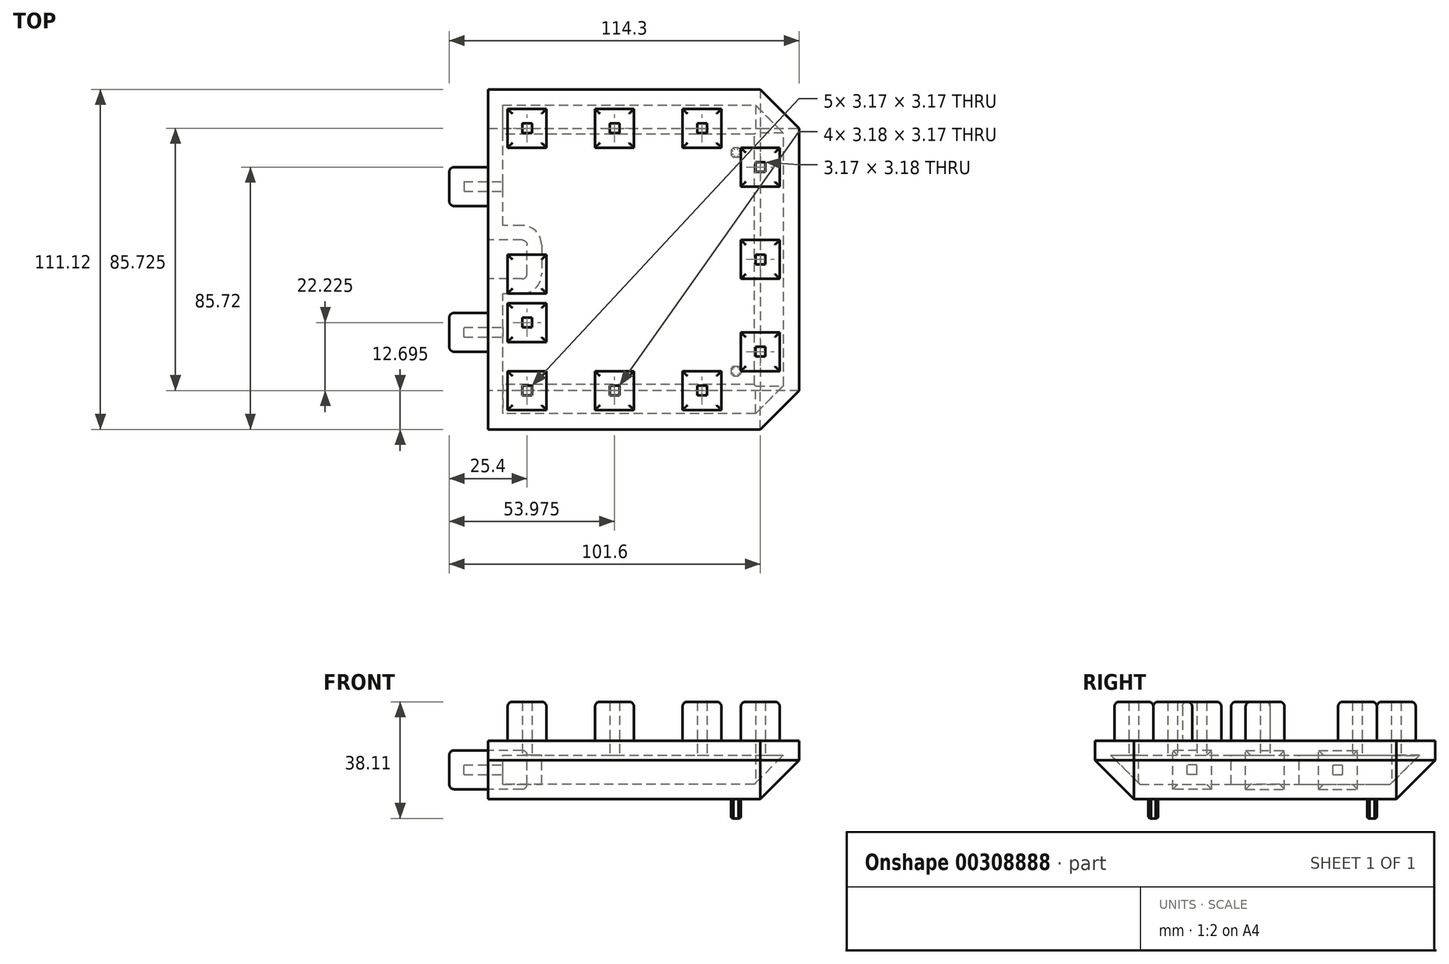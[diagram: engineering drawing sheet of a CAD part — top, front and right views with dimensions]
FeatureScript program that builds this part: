
annotation { "Feature Type Name" : "Feature", "Feature Type Description" : "" }
export const myFeature = defineFeature(function(context is Context, id is Id, definition is map)
    precondition{}
    {
        {
            var Q0;
            Q0=qCreatedBy(makeId("Front.planeOp"),FACE);
            var sketch = newSketch(context, id + "F0", { "sketchPlane" : qUnion([Q0])});
            skLineSegment(sketch, "E0.bottom", {"start": v(-50.8, -9.53) * mm, "end": v(50.8, -9.53) * mm});
            skLineSegment(sketch, "E0.top", {"start": v(-50.8, 9.53) * mm, "end": v(50.8, 9.53) * mm});
            skLineSegment(sketch, "E0.left", {"start": v(-50.8, -9.53) * mm, "end": v(-50.8, 9.53) * mm});
            skLineSegment(sketch, "E0.right", {"start": v(50.8, -9.53) * mm, "end": v(50.8, 9.53) * mm});
            skPoint(sketch, "E0.middle", {"position": v(0, 0) * mm});
            skSolve(sketch);
        }
        {
            var Q0;
            Q0 = qSketchRegion(id + "F0", true);
            extrude(context, id + "F1", {"entities" : qUnion([Q0]), "depth" : 111.12 * mm});
        }
        {
            var Q0;
            Q0=makeQuery(id+"F1.opExtrude","SWEPT_EDGE",EDGE,{"disambiguationData":[OSD([sQuery(id+"F0.wireOp",EDGE,"E0.bottom"),sQuery(id+"F0.wireOp",EDGE,"E0.right")])]});
            var Q1;
            Q1=makeQuery(id+"F1.opExtrude","CAP_EDGE",EDGE,{"disambiguationData":[OSD([sQuery(id+"F0.wireOp",EDGE,"E0.bottom")])],"isStart":false});
            var Q2;
            Q2=makeQuery(id+"F1.opExtrude","CAP_EDGE",EDGE,{"disambiguationData":[OSD([sQuery(id+"F0.wireOp",EDGE,"E0.bottom")])],"isStart":true});
            var Q3;
            Q3=makeQuery(id+"F1.opExtrude","CAP_EDGE",EDGE,{"disambiguationData":[OSD([sQuery(id+"F0.wireOp",EDGE,"E0.right")])],"isStart":false});
            var Q4;
            Q4=makeQuery(id+"F1.opExtrude","CAP_EDGE",EDGE,{"disambiguationData":[OSD([sQuery(id+"F0.wireOp",EDGE,"E0.right")])],"isStart":true});
            chamfer(context, id + "F2", {"entities" : qUnion([Q0, Q1, Q2, Q3, Q4]), "width" : 12.7 * mm, "tangentPropagation" : true});
        }
        {
            var Q0;
            Q0=makeQuery(id+"F1.opExtrude","SWEPT_FACE",FACE,{"disambiguationData":[OSD([sQuery(id+"F0.wireOp",EDGE,"E0.top")])]});
            var sketch = newSketch(context, id + "F3", { "sketchPlane" : qUnion([Q0])});
            skLineSegment(sketch, "E1.bottom", {"start": v(31.75, -31.75) * mm, "end": v(44.45, -31.75) * mm});
            skLineSegment(sketch, "E1.top", {"start": v(31.75, -19.05) * mm, "end": v(44.45, -19.05) * mm});
            skLineSegment(sketch, "E1.left", {"start": v(31.75, -31.75) * mm, "end": v(31.75, -19.05) * mm});
            skLineSegment(sketch, "E1.right", {"start": v(44.45, -31.75) * mm, "end": v(44.45, -19.05) * mm});
            skPoint(sketch, "E1.middle", {"position": v(38.1, -25.4) * mm});
            skLineSegment(sketch, "E2.bottom", {"start": v(31.75, -92.08) * mm, "end": v(44.45, -92.08) * mm});
            skLineSegment(sketch, "E2.top", {"start": v(31.75, -79.38) * mm, "end": v(44.45, -79.38) * mm});
            skLineSegment(sketch, "E2.left", {"start": v(31.75, -92.08) * mm, "end": v(31.75, -79.38) * mm});
            skLineSegment(sketch, "E2.right", {"start": v(44.45, -92.08) * mm, "end": v(44.45, -79.38) * mm});
            skPoint(sketch, "E2.middle", {"position": v(38.1, -85.73) * mm});
            skLineSegment(sketch, "E3.bottom", {"start": v(31.75, -61.91) * mm, "end": v(44.45, -61.91) * mm});
            skLineSegment(sketch, "E3.top", {"start": v(31.75, -49.21) * mm, "end": v(44.45, -49.21) * mm});
            skLineSegment(sketch, "E3.left", {"start": v(31.75, -61.91) * mm, "end": v(31.75, -49.21) * mm});
            skLineSegment(sketch, "E3.right", {"start": v(44.45, -61.91) * mm, "end": v(44.45, -49.21) * mm});
            skPoint(sketch, "E3.middle", {"position": v(38.1, -55.56) * mm});
            skLineSegment(sketch, "E4.bottom", {"start": v(12.7, -19.05) * mm, "end": v(25.4, -19.05) * mm});
            skLineSegment(sketch, "E4.top", {"start": v(12.7, -6.35) * mm, "end": v(25.4, -6.35) * mm});
            skLineSegment(sketch, "E4.left", {"start": v(12.7, -19.05) * mm, "end": v(12.7, -6.35) * mm});
            skLineSegment(sketch, "E4.right", {"start": v(25.4, -19.05) * mm, "end": v(25.4, -6.35) * mm});
            skPoint(sketch, "E4.middle", {"position": v(19.05, -12.7) * mm});
            skLineSegment(sketch, "E5.bottom", {"start": v(12.7, -92.08) * mm, "end": v(25.4, -92.08) * mm});
            skLineSegment(sketch, "E5.top", {"start": v(12.7, -104.78) * mm, "end": v(25.4, -104.78) * mm});
            skLineSegment(sketch, "E5.left", {"start": v(12.7, -92.08) * mm, "end": v(12.7, -104.78) * mm});
            skLineSegment(sketch, "E5.right", {"start": v(25.4, -92.08) * mm, "end": v(25.4, -104.78) * mm});
            skPoint(sketch, "E5.middle", {"position": v(19.05, -98.43) * mm});
            skLineSegment(sketch, "E6.bottom", {"start": v(-15.88, -19.05) * mm, "end": v(-3.18, -19.05) * mm});
            skLineSegment(sketch, "E6.top", {"start": v(-15.88, -6.35) * mm, "end": v(-3.18, -6.35) * mm});
            skLineSegment(sketch, "E6.left", {"start": v(-15.88, -19.05) * mm, "end": v(-15.88, -6.35) * mm});
            skLineSegment(sketch, "E6.right", {"start": v(-3.18, -19.05) * mm, "end": v(-3.18, -6.35) * mm});
            skPoint(sketch, "E6.middle", {"position": v(-9.53, -12.7) * mm});
            skLineSegment(sketch, "E7.bottom", {"start": v(-15.88, -92.08) * mm, "end": v(-3.18, -92.08) * mm});
            skLineSegment(sketch, "E7.top", {"start": v(-15.88, -104.78) * mm, "end": v(-3.18, -104.78) * mm});
            skLineSegment(sketch, "E7.left", {"start": v(-15.88, -92.08) * mm, "end": v(-15.88, -104.78) * mm});
            skLineSegment(sketch, "E7.right", {"start": v(-3.18, -92.08) * mm, "end": v(-3.18, -104.78) * mm});
            skPoint(sketch, "E7.middle", {"position": v(-9.53, -98.43) * mm});
            skLineSegment(sketch, "E8.bottom", {"start": v(-31.75, -19.05) * mm, "end": v(-44.45, -19.05) * mm});
            skLineSegment(sketch, "E8.top", {"start": v(-31.75, -6.35) * mm, "end": v(-44.45, -6.35) * mm});
            skLineSegment(sketch, "E8.left", {"start": v(-31.75, -19.05) * mm, "end": v(-31.75, -6.35) * mm});
            skLineSegment(sketch, "E8.right", {"start": v(-44.45, -19.05) * mm, "end": v(-44.45, -6.35) * mm});
            skPoint(sketch, "E8.middle", {"position": v(-38.1, -12.7) * mm});
            skPoint(sketch, "E8.middle.positionSnap0", {"position": v(-15.88, -12.7) * mm});
            skPoint(sketch, "E8.centerSnap0", {"position": v(-15.88, -12.7) * mm});
            skLineSegment(sketch, "E9.bottom", {"start": v(-31.75, -104.78) * mm, "end": v(-44.45, -104.78) * mm});
            skLineSegment(sketch, "E9.top", {"start": v(-31.75, -92.08) * mm, "end": v(-44.45, -92.08) * mm});
            skLineSegment(sketch, "E9.left", {"start": v(-31.75, -104.78) * mm, "end": v(-31.75, -92.08) * mm});
            skLineSegment(sketch, "E9.right", {"start": v(-44.45, -104.78) * mm, "end": v(-44.45, -92.08) * mm});
            skPoint(sketch, "E9.middle", {"position": v(-38.1, -98.43) * mm});
            skPoint(sketch, "E9.middle.positionSnap0", {"position": v(-15.88, -98.43) * mm});
            skPoint(sketch, "E9.centerSnap0", {"position": v(-15.88, -98.43) * mm});
            skSolve(sketch);
        }
        {
            var Q0;
            Q0 = qSketchRegion(id + "F3", true);
            extrude(context, id + "F4", {"entities" : qUnion([Q0]), "operationType" : NewBodyOperationType.ADD, "depth" : 12.7 * mm});
        }
        {
            var Q0;
            Q0=makeQuery(id+"F1.opExtrude","SWEPT_FACE",FACE,{"disambiguationData":[OSD([sQuery(id+"F0.wireOp",EDGE,"E0.bottom")])]});
            var sketch = newSketch(context, id + "F5", { "sketchPlane" : qUnion([Q0])});
            skLineSegment(sketch, "E10.bottom", {"start": v(28.58, 90.49) * mm, "end": v(31.75, 90.49) * mm});
            skLineSegment(sketch, "E10.top", {"start": v(28.58, 93.66) * mm, "end": v(31.75, 93.66) * mm});
            skLineSegment(sketch, "E10.left", {"start": v(28.58, 90.49) * mm, "end": v(28.58, 93.66) * mm});
            skLineSegment(sketch, "E10.right", {"start": v(31.75, 90.49) * mm, "end": v(31.75, 93.66) * mm});
            skPoint(sketch, "E10.middle", {"position": v(30.16, 92.08) * mm});
            skLineSegment(sketch, "E11.bottom", {"start": v(31.75, 19.05) * mm, "end": v(28.58, 19.05) * mm});
            skLineSegment(sketch, "E11.top", {"start": v(31.75, 22.22) * mm, "end": v(28.58, 22.22) * mm});
            skLineSegment(sketch, "E11.left", {"start": v(31.75, 19.05) * mm, "end": v(31.75, 22.23) * mm});
            skLineSegment(sketch, "E11.right", {"start": v(28.58, 19.05) * mm, "end": v(28.58, 22.23) * mm});
            skPoint(sketch, "E11.middle", {"position": v(30.16, 20.64) * mm});
            skSolve(sketch);
        }
        {
            var Q0;
            Q0 = qSketchRegion(id + "F5", true);
            extrude(context, id + "F6", {"entities" : qUnion([Q0]), "operationType" : NewBodyOperationType.ADD, "depth" : 6.35 * mm});
        }
        {
            var Q0;
            Q0=makeQuery(id+"F6.opExtrude","SWEPT_EDGE",EDGE,{"disambiguationData":[OSD([sQuery(id+"F5.wireOp",EDGE,"E11.bottom"),sQuery(id+"F5.wireOp",EDGE,"E11.right")])]});
            var Q1;
            Q1=makeQuery(id+"F6.opExtrude","SWEPT_EDGE",EDGE,{"disambiguationData":[OSD([sQuery(id+"F5.wireOp",EDGE,"E11.top"),sQuery(id+"F5.wireOp",EDGE,"E11.right")])]});
            var Q2;
            Q2=makeQuery(id+"F6.opExtrude","SWEPT_EDGE",EDGE,{"disambiguationData":[OSD([sQuery(id+"F5.wireOp",EDGE,"E11.top"),sQuery(id+"F5.wireOp",EDGE,"E11.left")])]});
            var Q3;
            Q3=makeQuery(id+"F6.opExtrude","SWEPT_EDGE",EDGE,{"disambiguationData":[OSD([sQuery(id+"F5.wireOp",EDGE,"E11.bottom"),sQuery(id+"F5.wireOp",EDGE,"E11.left")])]});
            var Q4;
            Q4=makeQuery(id+"F6.opExtrude","CAP_EDGE",EDGE,{"disambiguationData":[OSD([sQuery(id+"F5.wireOp",EDGE,"E11.left")])],"isStart":true});
            var Q5;
            Q5=makeQuery(id+"F6.opExtrude","SWEPT_EDGE",EDGE,{"disambiguationData":[OSD([sQuery(id+"F5.wireOp",EDGE,"E10.bottom"),sQuery(id+"F5.wireOp",EDGE,"E10.left")])]});
            var Q6;
            Q6=makeQuery(id+"F6.opExtrude","SWEPT_EDGE",EDGE,{"disambiguationData":[OSD([sQuery(id+"F5.wireOp",EDGE,"E10.bottom"),sQuery(id+"F5.wireOp",EDGE,"E10.right")])]});
            var Q7;
            Q7=makeQuery(id+"F6.opExtrude","SWEPT_EDGE",EDGE,{"disambiguationData":[OSD([sQuery(id+"F5.wireOp",EDGE,"E10.top"),sQuery(id+"F5.wireOp",EDGE,"E10.right")])]});
            var Q8;
            Q8=makeQuery(id+"F6.opExtrude","CAP_EDGE",EDGE,{"disambiguationData":[OSD([sQuery(id+"F5.wireOp",EDGE,"E10.right")])],"isStart":true});
            var Q9;
            Q9=makeQuery(id+"F6.opExtrude","SWEPT_EDGE",EDGE,{"disambiguationData":[OSD([sQuery(id+"F5.wireOp",EDGE,"E10.top"),sQuery(id+"F5.wireOp",EDGE,"E10.left")])]});
            chamfer(context, id + "F7", {"entities" : qUnion([Q0, Q1, Q2, Q3, Q4, Q5, Q6, Q7, Q8, Q9]), "width" : 0.8 * mm, "tangentPropagation" : true});
        }
        {
            var Q0;
            Q0=makeQuery(id+"F6.opExtrude","CAP_FACE",FACE,{"disambiguationData":[OSD([sQuery(id+"F5.wireOp",EDGE,"E10.bottom"),sQuery(id+"F5.wireOp",EDGE,"E10.top"),sQuery(id+"F5.wireOp",EDGE,"E10.left"),sQuery(id+"F5.wireOp",EDGE,"E10.right")])],"isStart":false});
            var Q1;
            Q1=makeQuery(id+"F6.opExtrude","CAP_FACE",FACE,{"disambiguationData":[OSD([sQuery(id+"F5.wireOp",EDGE,"E11.bottom"),sQuery(id+"F5.wireOp",EDGE,"E11.top"),sQuery(id+"F5.wireOp",EDGE,"E11.left"),sQuery(id+"F5.wireOp",EDGE,"E11.right")])],"isStart":false});
            fillet(context, id + "F8", {"entities" : qUnion([Q0, Q1]), "radius" : 0.64 * mm, "tangentPropagation" : true, "allowEdgeOverflow" : false});
        }
        {
            var Q0;
            Q0=makeQuery(id+"F1.opExtrude","SWEPT_FACE",FACE,{"disambiguationData":[OSD([sQuery(id+"F0.wireOp",EDGE,"E0.left")])]});
            var sketch = newSketch(context, id + "F9", { "sketchPlane" : qUnion([Q0])});
            skLineSegment(sketch, "E12.bottom", {"start": v(38.1, -6.35) * mm, "end": v(25.4, -6.35) * mm});
            skLineSegment(sketch, "E12.top", {"start": v(38.1, 6.35) * mm, "end": v(25.4, 6.35) * mm});
            skLineSegment(sketch, "E12.left", {"start": v(38.1, -6.35) * mm, "end": v(38.1, 6.35) * mm});
            skLineSegment(sketch, "E12.right", {"start": v(25.4, -6.35) * mm, "end": v(25.4, 6.35) * mm});
            skPoint(sketch, "E12.middle", {"position": v(31.75, 0) * mm});
            skLineSegment(sketch, "E13.bottom", {"start": v(73.03, -6.35) * mm, "end": v(85.73, -6.35) * mm});
            skLineSegment(sketch, "E13.top", {"start": v(73.03, 6.35) * mm, "end": v(85.73, 6.35) * mm});
            skLineSegment(sketch, "E13.left", {"start": v(73.03, -6.35) * mm, "end": v(73.03, 6.35) * mm});
            skLineSegment(sketch, "E13.right", {"start": v(85.73, -6.35) * mm, "end": v(85.73, 6.35) * mm});
            skPoint(sketch, "E13.middle", {"position": v(79.38, 0) * mm});
            skLineSegment(sketch, "E14.bottom", {"start": v(61.91, -6.35) * mm, "end": v(49.21, -6.35) * mm});
            skLineSegment(sketch, "E14.top", {"start": v(61.91, 6.35) * mm, "end": v(49.21, 6.35) * mm});
            skLineSegment(sketch, "E14.left", {"start": v(61.91, -6.35) * mm, "end": v(61.91, 6.35) * mm});
            skLineSegment(sketch, "E14.right", {"start": v(49.21, -6.35) * mm, "end": v(49.21, 6.35) * mm});
            skPoint(sketch, "E14.middle", {"position": v(55.56, 0) * mm});
            skSolve(sketch);
        }
        {
            var Q0;
            Q0=makeQuery(id+"F9.imprint","IMPRINT",FACE,{"disambiguationData":[TD([[makeQuery(id+"F9.imprint","IMPRINT",EDGE,{"derivedFrom":sQuery(id+"F9.wireOp",EDGE,"E12.bottom")}),-1.0]])]});
            var Q1;
            Q1=makeQuery(id+"F9.imprint","IMPRINT",FACE,{"disambiguationData":[TD([[makeQuery(id+"F9.imprint","IMPRINT",EDGE,{"derivedFrom":sQuery(id+"F9.wireOp",EDGE,"E13.bottom")}),1.0]])]});
            extrude(context, id + "F10", {"entities" : qUnion([Q0, Q1]), "operationType" : NewBodyOperationType.ADD, "depth" : 12.7 * mm});
        }
        {
            var Q0;
            Q0=makeQuery(id+"F9.imprint","IMPRINT",FACE,{"disambiguationData":[TD([[makeQuery(id+"F9.imprint","IMPRINT",EDGE,{"derivedFrom":sQuery(id+"F9.wireOp",EDGE,"E14.bottom")}),-1.0]])]});
            extrude(context, id + "F11", {"entities" : qUnion([Q0]), "operationType" : NewBodyOperationType.REMOVE, "oppositeDirection" : true, "depth" : 12.7 * mm});
        }
        {
            var Q0;
            Q0=makeQuery(id+"F1.opExtrude","SWEPT_FACE",FACE,{"disambiguationData":[OSD([sQuery(id+"F0.wireOp",EDGE,"E0.top")])]});
            var sketch = newSketch(context, id + "F12", { "sketchPlane" : qUnion([Q0])});
            skLineSegment(sketch, "E15", {"start": v(-50.8, -85.73) * mm, "end": v(25.4, -85.73) * mm});
            skLineSegment(sketch, "E16", {"start": v(25.4, -85.73) * mm, "end": v(25.4, -25.4) * mm});
            skLineSegment(sketch, "E17", {"start": v(25.4, -25.4) * mm, "end": v(-50.8, -25.4) * mm});
            skLineSegment(sketch, "E18.bottom", {"start": v(-50.8, -85.73) * mm, "end": v(-25.4, -85.73) * mm});
            skLineSegment(sketch, "E18.top", {"start": v(-50.8, -50.8) * mm, "end": v(-25.4, -50.8) * mm});
            skLineSegment(sketch, "E18.left", {"start": v(-50.8, -85.73) * mm, "end": v(-50.8, -50.8) * mm});
            skLineSegment(sketch, "E18.right", {"start": v(-25.4, -85.73) * mm, "end": v(-25.4, -50.8) * mm});
            skLineSegment(sketch, "E19.bottom", {"start": v(-31.75, -66.68) * mm, "end": v(-44.45, -66.68) * mm});
            skLineSegment(sketch, "E19.top", {"start": v(-31.75, -53.97) * mm, "end": v(-44.45, -53.97) * mm});
            skLineSegment(sketch, "E19.left", {"start": v(-31.75, -66.68) * mm, "end": v(-31.75, -53.97) * mm});
            skLineSegment(sketch, "E19.right", {"start": v(-44.45, -66.68) * mm, "end": v(-44.45, -53.97) * mm});
            skPoint(sketch, "E19.middle", {"position": v(-38.1, -60.33) * mm});
            skLineSegment(sketch, "E20.bottom", {"start": v(-31.75, -82.55) * mm, "end": v(-44.45, -82.55) * mm});
            skLineSegment(sketch, "E20.top", {"start": v(-31.75, -69.85) * mm, "end": v(-44.45, -69.85) * mm});
            skLineSegment(sketch, "E20.left", {"start": v(-31.75, -82.55) * mm, "end": v(-31.75, -69.85) * mm});
            skLineSegment(sketch, "E20.right", {"start": v(-44.45, -82.55) * mm, "end": v(-44.45, -69.85) * mm});
            skPoint(sketch, "E20.middle", {"position": v(-38.1, -76.2) * mm});
            skSolve(sketch);
        }
        {
            var Q0;
            Q0=makeQuery(id+"F12.imprint","IMPRINT",FACE,{"disambiguationData":[TD([[makeQuery(id+"F12.imprint","IMPRINT",EDGE,{"derivedFrom":sQuery(id+"F12.wireOp",EDGE,"E19.bottom")}),-1.0]])]});
            var Q1;
            Q1=makeQuery(id+"F12.imprint","IMPRINT",FACE,{"disambiguationData":[TD([[makeQuery(id+"F12.imprint","IMPRINT",EDGE,{"derivedFrom":sQuery(id+"F12.wireOp",EDGE,"E20.bottom")}),-1.0]])]});
            extrude(context, id + "F13", {"entities" : qUnion([Q0, Q1]), "operationType" : NewBodyOperationType.ADD, "depth" : 12.7 * mm});
        }
        {
            var Q0;
            Q0=makeQuery(id+"F4.opExtrude","CAP_FACE",FACE,{"disambiguationData":[OSD([sQuery(id+"F3.wireOp",EDGE,"E1.bottom"),sQuery(id+"F3.wireOp",EDGE,"E1.top"),sQuery(id+"F3.wireOp",EDGE,"E1.left"),sQuery(id+"F3.wireOp",EDGE,"E1.right")])],"isStart":false});
            var Q1;
            Q1=makeQuery(id+"F4.opExtrude","CAP_FACE",FACE,{"disambiguationData":[OSD([sQuery(id+"F3.wireOp",EDGE,"E3.bottom"),sQuery(id+"F3.wireOp",EDGE,"E3.top"),sQuery(id+"F3.wireOp",EDGE,"E3.left"),sQuery(id+"F3.wireOp",EDGE,"E3.right")])],"isStart":false});
            var Q2;
            Q2=makeQuery(id+"F4.opExtrude","CAP_FACE",FACE,{"disambiguationData":[OSD([sQuery(id+"F3.wireOp",EDGE,"E2.bottom"),sQuery(id+"F3.wireOp",EDGE,"E2.top"),sQuery(id+"F3.wireOp",EDGE,"E2.left"),sQuery(id+"F3.wireOp",EDGE,"E2.right")])],"isStart":false});
            var Q3;
            Q3=makeQuery(id+"F4.opExtrude","CAP_FACE",FACE,{"disambiguationData":[OSD([sQuery(id+"F3.wireOp",EDGE,"E4.bottom"),sQuery(id+"F3.wireOp",EDGE,"E4.top"),sQuery(id+"F3.wireOp",EDGE,"E4.left"),sQuery(id+"F3.wireOp",EDGE,"E4.right")])],"isStart":false});
            var Q4;
            Q4=makeQuery(id+"F4.opExtrude","CAP_FACE",FACE,{"disambiguationData":[OSD([sQuery(id+"F3.wireOp",EDGE,"E6.bottom"),sQuery(id+"F3.wireOp",EDGE,"E6.top"),sQuery(id+"F3.wireOp",EDGE,"E6.left"),sQuery(id+"F3.wireOp",EDGE,"E6.right")])],"isStart":false});
            var Q5;
            Q5=makeQuery(id+"F4.opExtrude","CAP_FACE",FACE,{"disambiguationData":[OSD([sQuery(id+"F3.wireOp",EDGE,"E7.bottom"),sQuery(id+"F3.wireOp",EDGE,"E7.top"),sQuery(id+"F3.wireOp",EDGE,"E7.left"),sQuery(id+"F3.wireOp",EDGE,"E7.right")])],"isStart":false});
            var Q6;
            Q6=makeQuery(id+"F4.opExtrude","CAP_FACE",FACE,{"disambiguationData":[OSD([sQuery(id+"F3.wireOp",EDGE,"E5.bottom"),sQuery(id+"F3.wireOp",EDGE,"E5.top"),sQuery(id+"F3.wireOp",EDGE,"E5.left"),sQuery(id+"F3.wireOp",EDGE,"E5.right")])],"isStart":false});
            var Q7;
            Q7=makeQuery(id+"F4.opExtrude","CAP_FACE",FACE,{"disambiguationData":[OSD([sQuery(id+"F3.wireOp",EDGE,"E9.bottom"),sQuery(id+"F3.wireOp",EDGE,"E9.top"),sQuery(id+"F3.wireOp",EDGE,"E9.left"),sQuery(id+"F3.wireOp",EDGE,"E9.right")])],"isStart":false});
            var Q8;
            Q8=makeQuery(id+"F4.opExtrude","CAP_FACE",FACE,{"disambiguationData":[OSD([sQuery(id+"F3.wireOp",EDGE,"E8.bottom"),sQuery(id+"F3.wireOp",EDGE,"E8.top"),sQuery(id+"F3.wireOp",EDGE,"E8.left"),sQuery(id+"F3.wireOp",EDGE,"E8.right")])],"isStart":false});
            var Q9;
            Q9=makeQuery(id+"F10.opExtrude","CAP_FACE",FACE,{"disambiguationData":[OSD([sQuery(id+"F9.wireOp",EDGE,"E12.bottom"),sQuery(id+"F9.wireOp",EDGE,"E12.top"),sQuery(id+"F9.wireOp",EDGE,"E12.left"),sQuery(id+"F9.wireOp",EDGE,"E12.right")])],"isStart":false});
            var Q10;
            Q10=makeQuery(id+"F11.boolean.opBoolean","COPY",FACE,{"derivedFrom":makeQuery(id+"F11.opExtrude","CAP_FACE",FACE,{"disambiguationData":[OSD([sQuery(id+"F9.wireOp",EDGE,"E14.bottom"),sQuery(id+"F9.wireOp",EDGE,"E14.top"),sQuery(id+"F9.wireOp",EDGE,"E14.left"),sQuery(id+"F9.wireOp",EDGE,"E14.right")])],"isStart":false})});
            var Q11;
            Q11=makeQuery(id+"F10.opExtrude","CAP_FACE",FACE,{"disambiguationData":[OSD([sQuery(id+"F9.wireOp",EDGE,"E13.bottom"),sQuery(id+"F9.wireOp",EDGE,"E13.top"),sQuery(id+"F9.wireOp",EDGE,"E13.left"),sQuery(id+"F9.wireOp",EDGE,"E13.right")])],"isStart":false});
            var Q12;
            Q12=makeQuery(id+"F13.opExtrude","CAP_FACE",FACE,{"disambiguationData":[OSD([sQuery(id+"F12.wireOp",EDGE,"E19.bottom"),sQuery(id+"F12.wireOp",EDGE,"E19.top"),sQuery(id+"F12.wireOp",EDGE,"E19.left"),sQuery(id+"F12.wireOp",EDGE,"E19.right")])],"isStart":false});
            var Q13;
            Q13=makeQuery(id+"F13.opExtrude","CAP_FACE",FACE,{"disambiguationData":[OSD([sQuery(id+"F12.wireOp",EDGE,"E20.bottom"),sQuery(id+"F12.wireOp",EDGE,"E20.top"),sQuery(id+"F12.wireOp",EDGE,"E20.left"),sQuery(id+"F12.wireOp",EDGE,"E20.right")])],"isStart":false});
            fillet(context, id + "F14", {"entities" : qUnion([Q0, Q1, Q2, Q3, Q4, Q5, Q6, Q7, Q8, Q9, Q10, Q11, Q12, Q13]), "radius" : 1.59 * mm, "tangentPropagation" : true, "allowEdgeOverflow" : false});
        }
        {
            var Q0;
            Q0=makeQuery(id+"F4.opExtrude","CAP_FACE",FACE,{"disambiguationData":[OSD([sQuery(id+"F3.wireOp",EDGE,"E3.bottom"),sQuery(id+"F3.wireOp",EDGE,"E3.top"),sQuery(id+"F3.wireOp",EDGE,"E3.left"),sQuery(id+"F3.wireOp",EDGE,"E3.right")])],"isStart":false});
            var Q1;
            Q1=makeQuery(id+"F4.opExtrude","CAP_FACE",FACE,{"disambiguationData":[OSD([sQuery(id+"F3.wireOp",EDGE,"E2.bottom"),sQuery(id+"F3.wireOp",EDGE,"E2.top"),sQuery(id+"F3.wireOp",EDGE,"E2.left"),sQuery(id+"F3.wireOp",EDGE,"E2.right")])],"isStart":false});
            var Q2;
            Q2=makeQuery(id+"F4.opExtrude","CAP_FACE",FACE,{"disambiguationData":[OSD([sQuery(id+"F3.wireOp",EDGE,"E5.bottom"),sQuery(id+"F3.wireOp",EDGE,"E5.top"),sQuery(id+"F3.wireOp",EDGE,"E5.left"),sQuery(id+"F3.wireOp",EDGE,"E5.right")])],"isStart":false});
            var Q3;
            Q3=makeQuery(id+"F4.opExtrude","CAP_FACE",FACE,{"disambiguationData":[OSD([sQuery(id+"F3.wireOp",EDGE,"E7.bottom"),sQuery(id+"F3.wireOp",EDGE,"E7.top"),sQuery(id+"F3.wireOp",EDGE,"E7.left"),sQuery(id+"F3.wireOp",EDGE,"E7.right")])],"isStart":false});
            var Q4;
            Q4=makeQuery(id+"F4.opExtrude","CAP_FACE",FACE,{"disambiguationData":[OSD([sQuery(id+"F3.wireOp",EDGE,"E1.bottom"),sQuery(id+"F3.wireOp",EDGE,"E1.top"),sQuery(id+"F3.wireOp",EDGE,"E1.left"),sQuery(id+"F3.wireOp",EDGE,"E1.right")])],"isStart":false});
            var Q5;
            Q5=makeQuery(id+"F4.opExtrude","CAP_FACE",FACE,{"disambiguationData":[OSD([sQuery(id+"F3.wireOp",EDGE,"E4.bottom"),sQuery(id+"F3.wireOp",EDGE,"E4.top"),sQuery(id+"F3.wireOp",EDGE,"E4.left"),sQuery(id+"F3.wireOp",EDGE,"E4.right")])],"isStart":false});
            var Q6;
            Q6=makeQuery(id+"F4.opExtrude","CAP_FACE",FACE,{"disambiguationData":[OSD([sQuery(id+"F3.wireOp",EDGE,"E6.bottom"),sQuery(id+"F3.wireOp",EDGE,"E6.top"),sQuery(id+"F3.wireOp",EDGE,"E6.left"),sQuery(id+"F3.wireOp",EDGE,"E6.right")])],"isStart":false});
            var Q7;
            Q7=makeQuery(id+"F4.opExtrude","CAP_FACE",FACE,{"disambiguationData":[OSD([sQuery(id+"F3.wireOp",EDGE,"E8.bottom"),sQuery(id+"F3.wireOp",EDGE,"E8.top"),sQuery(id+"F3.wireOp",EDGE,"E8.left"),sQuery(id+"F3.wireOp",EDGE,"E8.right")])],"isStart":false});
            var Q8;
            Q8=makeQuery(id+"F13.opExtrude","CAP_FACE",FACE,{"disambiguationData":[OSD([sQuery(id+"F12.wireOp",EDGE,"E20.bottom"),sQuery(id+"F12.wireOp",EDGE,"E20.top"),sQuery(id+"F12.wireOp",EDGE,"E20.left"),sQuery(id+"F12.wireOp",EDGE,"E20.right")])],"isStart":false});
            var Q9;
            Q9=makeQuery(id+"F4.opExtrude","CAP_FACE",FACE,{"disambiguationData":[OSD([sQuery(id+"F3.wireOp",EDGE,"E9.bottom"),sQuery(id+"F3.wireOp",EDGE,"E9.top"),sQuery(id+"F3.wireOp",EDGE,"E9.left"),sQuery(id+"F3.wireOp",EDGE,"E9.right")])],"isStart":false});
            shell(context, id + "F15", {"entities" : qUnion([Q0, Q1, Q2, Q3, Q4, Q5, Q6, Q7, Q8, Q9]), "thickness" : 4.76 * mm});
        }
    });
